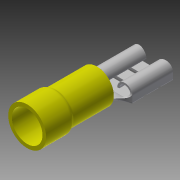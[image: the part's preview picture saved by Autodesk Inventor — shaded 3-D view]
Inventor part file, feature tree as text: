
AUTODESK INVENTOR PART (.ipt)
format: ipt  version: 2014 (Build 180170000, 170)  size: 522,752 bytes
history: native  units: in
note: dims shown in document units (in); Inventor stores cm internally (conversion verified against a paired STEP export)
features: sketch x13, extrude x10, projected_geometry x9, fillet x5, plane x3, shell x1, revolve x1, mirror x1, loft x1, chamfer x1
ambient origin geometry x8: Origin, YZ Plane, XZ Plane, XY Plane, X Axis, Y Axis, Z Axis, Center Point
bodies: Solid1 (feature_tree), Solid2 (feature_tree)
feature tree (45):
  extrude  "Extrusion1"  Depth=0.5in TaperAngle=0.0deg
  extrude  "Extrusion2"  Depth=0.03in TaperAngle=0.0deg
  fillet  "Fillet1"  Radius=0.02in
  fillet  "Fillet2"  Radius=0.03in
  shell  "Shell1"  Thickness=0.026in
  revolve  "Revolution1"  Angle=90.0deg
  plane  "Work Plane1"
  plane  "Work Plane2"
  extrude  "Extrusion3"  Depth=0.2905in
  mirror  "Mirror1"
  loft  "Loft2"
  fillet  "Fillet3"  Radius=0.109in
  chamfer  "Chamfer1"  Distance=0.291in
  extrude  "Extrusion4"  Depth=0.03in TaperAngle=45.0deg
  extrude  "Extrusion5"  Depth=0.3937in TaperAngle=90.0deg
  fillet  "Fillet4"  Radius=0.015in
  extrude  "Extrusion6"  Depth=0.015in TaperAngle=0.0deg
  extrude  "Extrusion7"  Depth=0.005in
  extrude  "Extrusion8"  Depth=0.003in TaperAngle=0.0deg
  fillet  "Fillet5"  Radius=0.003in
  plane  "Work Plane3"
  extrude  "Extrusion9"  Depth=0.005in
  extrude  "Extrusion10"  Depth=0.005in
  sketch  "Sketch1"  dims[d0=0.2415in d1=0.5in d2=0.0in]
  sketch  "Sketch2"  dims[d3=0.2715in d4=0.195in d5=0.0in d6=0.02in d7=0.03in d8=0.026in]
  projected_geometry  "Projected Loop1"
  sketch  "Sketch3"  dims[d9=0.014in d10=90.0deg]
  sketch  "Sketch5"  dims[d11=0.4in d12=0.2905in]
  sketch  "Sketch6"  dims[d13=0.0135in d14=0.037in d15=0.109in]
  projected_geometry  "Projected Loop2"
  sketch  "Sketch7"  dims[d16=0.01in d17=0.291in d18=0.0in]
  projected_geometry  "Projected Loop3"
  sketch  "Sketch8"  dims[d23=0.03in d24=0.003in d25=0.125in d26=45.0deg]
  projected_geometry  "Projected Loop4"
  sketch  "Sketch9"  dims[d27=0.0in d28=90.0deg d29=0.3937in d30=90.0deg d31=0.015in]
  projected_geometry  "Projected Loop5"
  sketch  "Sketch10"  dims[d32=0.291in d33=0.0in d34=0.015in d35=0.0in]
  projected_geometry  "Projected Loop6"
  sketch  "Sketch11"  dims[d36=0.005in d37=0.0235in]
  projected_geometry  "Projected Loop7"
  sketch  "Sketch12"  dims[d38=0.014in d39=0.0in d40=0.003in d41=0.0in d42=0.003in d43=0.0in]
  sketch  "Sketch14"  dims[d44=0.005in d45=0.01in]
  sketch  "Sketch15"  dims[d46=0.003in d47=0.0in d48=0.005in d49=0.05in d50=0.0in]
  projected_geometry  "Projected Loop8"
  projected_geometry  "Project Cut Edges1"
